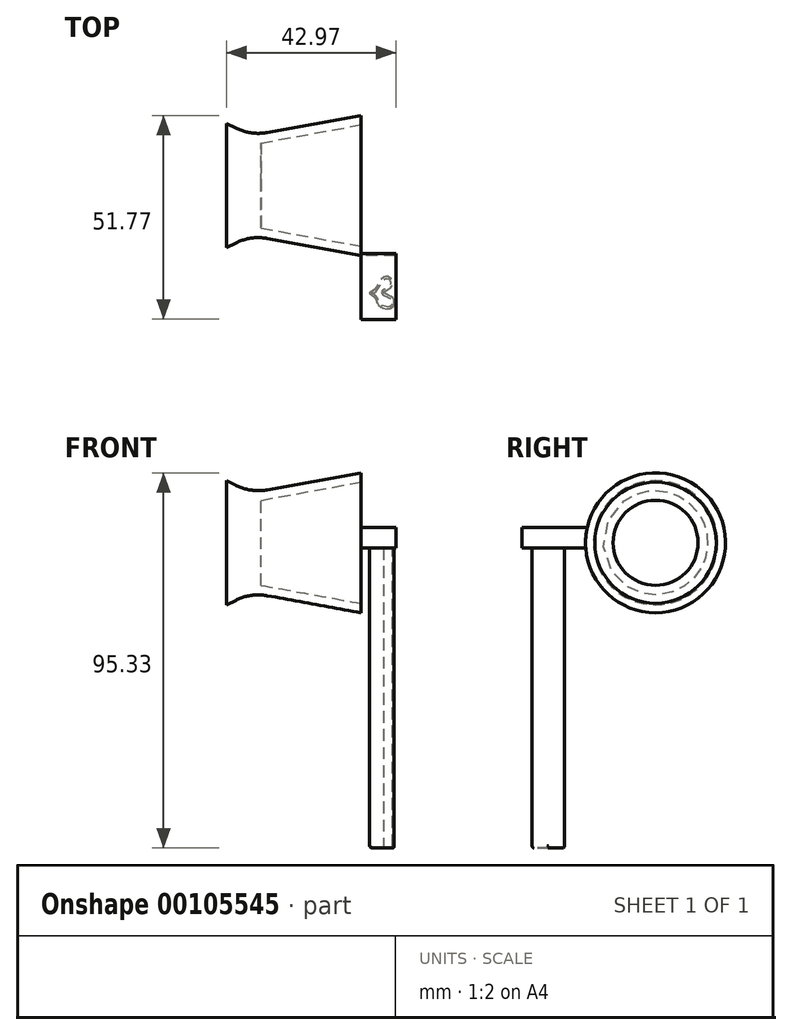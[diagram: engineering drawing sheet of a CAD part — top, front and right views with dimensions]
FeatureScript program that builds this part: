
annotation { "Feature Type Name" : "Feature", "Feature Type Description" : "" }
export const myFeature = defineFeature(function(context is Context, id is Id, definition is map)
    precondition{}
    {
        {
            var Q0;
            Q0=qCreatedBy(makeId("Top.planeOp"),FACE);
            var sketch = newSketch(context, id + "F0", { "sketchPlane" : qUnion([Q0])});
            skLineSegment(sketch, "E0", {"start": v(0, 0) * mm, "end": v(0, 12.7) * mm});
            skLineSegment(sketch, "E1", {"start": v(0, 12.7) * mm, "end": v(27.94, 17.78) * mm});
            skLineSegment(sketch, "E2", {"start": v(27.94, 17.78) * mm, "end": v(27.94, 15.41) * mm});
            skLineSegment(sketch, "E3", {"start": v(27.94, 15.41) * mm, "end": v(2.54, 10.8) * mm});
            skLineSegment(sketch, "E4", {"start": v(2.54, 10.8) * mm, "end": v(2.54, 0) * mm});
            skLineSegment(sketch, "E5", {"start": v(2.54, 0) * mm, "end": v(0, 0) * mm});
            skSolve(sketch);
        }
        {
            var Q0;
            Q0 = qSketchRegion(id + "F0", true);
            var Q1;
            Q1=sQuery(id+"F0.wireOp",EDGE,"E5");
            revolve(context, id + "F1", {"entities" : qUnion([Q0]), "axis" : qUnion([Q1]), "revolveType" : RevolveType.FULL});
        }
        {
            var Q0;
            Q0=qCreatedBy(makeId("Front.planeOp"),FACE);
            var sketch = newSketch(context, id + "F2", { "sketchPlane" : qUnion([Q0])});
            skLineSegment(sketch, "E6", {"start": v(0, 0) * mm, "end": v(0, 12.67) * mm});
            skLineSegment(sketch, "E7", {"start": v(0, 12.67) * mm, "end": v(-6.17, 15.77) * mm});
            skLineSegment(sketch, "E8", {"start": v(-6.17, 15.77) * mm, "end": v(-6.17, 0) * mm});
            skLineSegment(sketch, "E9", {"start": v(-6.17, 0) * mm, "end": v(0, 0) * mm});
            skSolve(sketch);
        }
        {
            var Q0;
            Q0=makeQuery(id+"F2.imprint","IMPRINT",FACE,{"disambiguationData":[TD([[makeQuery(id+"F2.imprint","IMPRINT",EDGE,{"derivedFrom":sQuery(id+"F2.wireOp",EDGE,"E6")}),1.0]])]});
            var Q1;
            Q1=sQuery(id+"F2.wireOp",EDGE,"E9");
            revolve(context, id + "F3", {"operationType" : NewBodyOperationType.ADD, "entities" : qUnion([Q0]), "axis" : qUnion([Q1]), "revolveType" : RevolveType.FULL});
        }
        {
            var Q0;
            Q0=makeQuery(id+"F1.opRevolve","SWEPT_EDGE",EDGE,{"disambiguationData":[OSD([sQuery(id+"F0.wireOp",EDGE,"E0"),sQuery(id+"F0.wireOp",EDGE,"E1")])]});
            fillet(context, id + "F4", {"entities" : qUnion([Q0]), "radius" : 12.7 * mm, "tangentPropagation" : true, "allowEdgeOverflow" : false});
        }
        {
            var Q0;
            {var subQ0=sQuery(id+"F0.wireOp",EDGE,"E1");Q0=makeQuery(id+"F4.opFillet","BLEND_EDGE",EDGE,{"blendedFrom":[makeQuery(id+"F1.opRevolve","SWEPT_EDGE",EDGE,{"disambiguationData":[OSD([sQuery(id+"F0.wireOp",EDGE,"E0"),subQ0])]}),makeQuery(id+"F1.opRevolve","SWEPT_FACE",FACE,{"disambiguationData":[OSD([subQ0])]})],"blendedInto":[makeQuery(id+"F1.opRevolve","SWEPT_FACE",FACE,{"disambiguationData":[OSD([subQ0])]})]});}
            var Q1;
            Q1=makeQuery(id+"F4.opFillet","BLEND_EDGE",EDGE,{"blendedFrom":[makeQuery(id+"F1.opRevolve","SWEPT_EDGE",EDGE,{"disambiguationData":[OSD([sQuery(id+"F0.wireOp",EDGE,"E0"),sQuery(id+"F0.wireOp",EDGE,"E1")])]}),makeQuery(id+"F3.opRevolve","SWEPT_FACE",FACE,{"disambiguationData":[OSD([sQuery(id+"F2.wireOp",EDGE,"E7")])]})],"blendedInto":[makeQuery(id+"F3.opRevolve","SWEPT_FACE",FACE,{"disambiguationData":[OSD([sQuery(id+"F2.wireOp",EDGE,"E7")])]})]});
            fillet(context, id + "F5", {"entities" : qUnion([Q0, Q1]), "radius" : 12.7 * mm, "tangentPropagation" : true, "allowEdgeOverflow" : false});
        }
        {
            var Q0;
            Q0=makeQuery(id+"F1.opRevolve","SWEPT_FACE",FACE,{"disambiguationData":[OSD([sQuery(id+"F0.wireOp",EDGE,"E2")])]});
            var sketch = newSketch(context, id + "F6", { "sketchPlane" : qUnion([Q0])});
            skLineSegment(sketch, "E10.bottom", {"start": v(-15.35, -1.35) * mm, "end": v(-34, -1.35) * mm});
            skLineSegment(sketch, "E10.top", {"start": v(-15.35, 3.93) * mm, "end": v(-34, 3.93) * mm});
            skLineSegment(sketch, "E10.left", {"start": v(-15.35, -1.35) * mm, "end": v(-15.35, 3.93) * mm});
            skLineSegment(sketch, "E10.right", {"start": v(-34, -1.35) * mm, "end": v(-34, 3.93) * mm});
            skSolve(sketch);
        }
        {
            var Q0;
            {var subQ0=sQuery(id+"F6.wireOp",EDGE,"E10.right");Q0=makeQuery(id+"F6.imprint","IMPRINT",FACE,{"disambiguationData":[TD([[makeQuery(id+"F6.imprint","IMPRINT",EDGE,{"derivedFrom":subQ0}),-1.0]])]});}
            extrude(context, id + "F7", {"entities" : qUnion([Q0]), "depth" : 8.86 * mm});
        }
        {
            var Q0;
            Q0=makeQuery(id+"F7.opExtrude","SWEPT_FACE",FACE,{"disambiguationData":[OSD([sQuery(id+"F6.wireOp",EDGE,"E10.bottom")])]});
            var sketch = newSketch(context, id + "F8", { "sketchPlane" : qUnion([Q0])});
            skFitSpline(sketch, "E11", {"points": [v(33.65, 27.18) * mm, v(35.57, 25.86) * mm, v(35.51, 23.54) * mm, v(33.35, 23.5) * mm, v(31.36, 26.55) * mm, v(30.14, 27.31) * mm, v(31.37, 28.34) * mm, v(32.12, 30.02) * mm, v(33.28, 30.97) * mm, v(35.73, 31.1) * mm, v(36.06, 28.64) * mm, v(33.65, 27.18) * mm]});
            skSolve(sketch);
        }
        {
            var Q0;
            Q0 = qSketchRegion(id + "F8", true);
            extrude(context, id + "F9", {"entities" : qUnion([Q0]), "operationType" : NewBodyOperationType.ADD, "depth" : 76.2 * mm});
        }
        {
            var Q0;
            Q0=makeQuery(id+"F9.opExtrude","CAP_EDGE",EDGE,{"disambiguationData":[OSD([sQuery(id+"F8.wireOp",EDGE,"E11")])],"isStart":false});
            fillet(context, id + "F10", {"entities" : qUnion([Q0]), "radius" : 0.5 * mm, "tangentPropagation" : true, "allowEdgeOverflow" : false});
        }
    });
